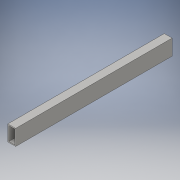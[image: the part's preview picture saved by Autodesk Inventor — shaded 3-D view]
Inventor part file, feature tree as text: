
AUTODESK INVENTOR PART (.ipt)
format: ipt  version: 2016 (Build 200138000, 138)  size: 92,672 bytes
history: native  units: in
note: dims shown in document units (in); Inventor stores cm internally (conversion verified against a paired STEP export)
features: extrude x1, sketch x1
ambient origin geometry x8: Origin, YZ Plane, XZ Plane, XY Plane, X Axis, Y Axis, Z Axis, Center Point
bodies: Solid1 (feature_tree)
feature tree (2):
  extrude  "Extrusion1"  Depth=2.0in
  sketch  "Sketch1"  dims[d0=1.0in d1=2.0in d2=0.125in d3=20.0in d4=0.0in]
